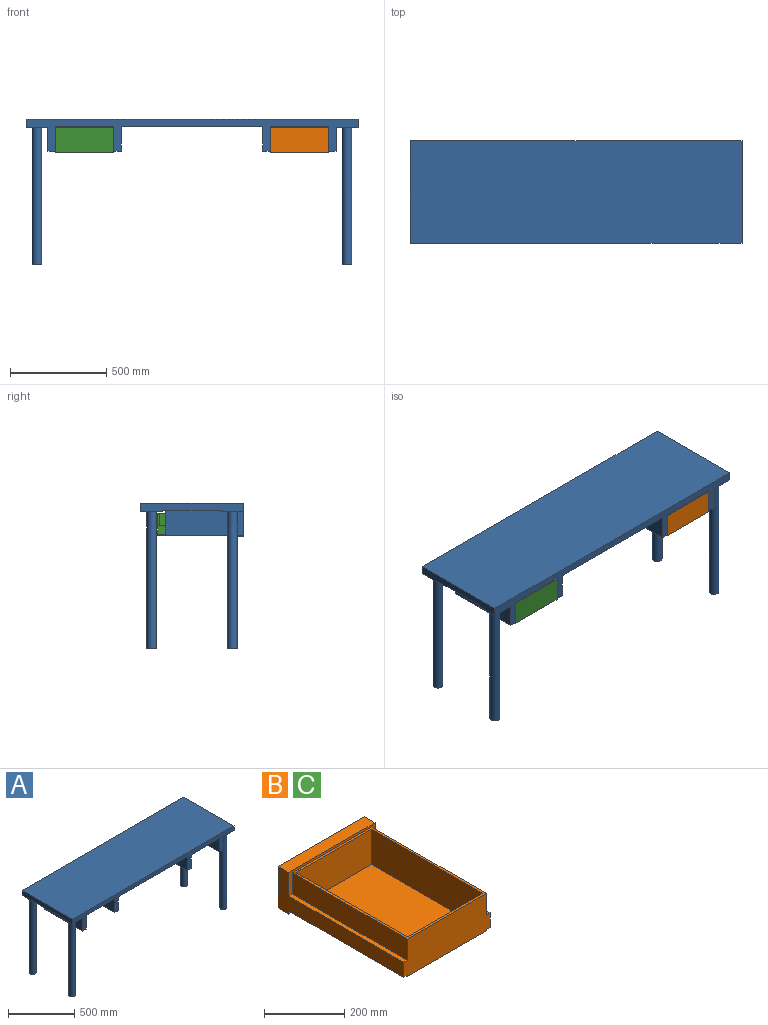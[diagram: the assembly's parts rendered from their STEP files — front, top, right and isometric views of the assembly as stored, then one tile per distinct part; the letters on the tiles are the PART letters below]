
ASSEMBLY  parts=3 mates=1
PART A: 40 faces, bbox 1727.2x533.4x755.7 mm
  f0: plane 406.4x127mm, normal (1,0,0), area 50887mm2, adj f1,f3,f15,f17,f18,f19
  f1: plane 1727.2x533.4mm, normal (0,0,-1), area 807095.2mm2, adj f0,f2,f3,f4,f5,f7,f11,f12
  f2: plane 533.4x44.45mm, normal (-1,0,0), area 21774.2mm2, adj f1,f3,f5,f6,f7,f8,f23,f24
  f3: plane 1727.2x165.1mm, normal (0,-1,0), area 86612.7mm2, adj f0,f1,f2,f4,f6,f8,f11,f13
  f4: plane 533.4x44.45mm, normal (1,0,0), area 21774.2mm2, adj f1,f3,f5,f6,f18,f19,f27,f29
  f5: plane 1727.2x44.45mm, normal (0,1,0), area 67257.9mm2, adj f1,f2,f4,f6,f22,f24,f28,f29
  f6: plane 1727.2x533.4mm, normal (0,0,1), area 921288.5mm2, adj f2,f3,f4,f5
  f7: plane 114.3x6.35mm, normal (0,1,0), area 725.8mm2, adj f1,f2,f8,f11
  f8: plane 114.3x114.3mm, normal (0,0,-1), area 11037.7mm2, adj f2,f3,f7,f9,f11
  f9: cylinder r=25.4mm len=711.2mm, axis (0,0,1), area 113502.5mm2, adj f8,f10
  f10: plane 50.8x50.8mm, normal (0,0,-1), area 2026.8mm2, adj f9
  f11: plane 406.4x127mm, normal (-1,0,0), area 50887mm2, adj f1,f3,f7,f8,f12,f14
  f12: plane 127x38.1mm, normal (0,1,0), area 4838.7mm2, adj f1,f11,f13,f14
  f13: plane 406.4x127mm, normal (1,0,0), area 51612.8mm2, adj f1,f3,f12,f14
  f14: plane 406.4x38.1mm, normal (0,0,-1), area 15483.8mm2, adj f3,f11,f12,f13
  f15: plane 127x38.1mm, normal (0,1,0), area 4838.7mm2, adj f0,f1,f16,f17
  f16: plane 406.4x127mm, normal (-1,0,0), area 51612.8mm2, adj f1,f3,f15,f17
  f17: plane 406.4x38.1mm, normal (0,0,-1), area 15483.8mm2, adj f0,f3,f15,f16
  f18: plane 114.3x6.35mm, normal (0,1,0), area 725.8mm2, adj f0,f1,f4,f19
  f19: plane 114.3x114.3mm, normal (0,0,-1), area 11037.7mm2, adj f0,f3,f4,f18,f20
  f20: cylinder r=25.4mm len=711.2mm, axis (0,0,1), area 113502.5mm2, adj f19,f21
  f21: plane 50.8x50.8mm, normal (0,0,-1), area 2026.8mm2, adj f20
  f22: plane 114.3x6.35mm, normal (1,0,0), area 725.8mm2, adj f1,f5,f23,f24
  f23: plane 114.3x6.35mm, normal (0,-1,0), area 725.8mm2, adj f1,f2,f22,f24
  f24: plane 114.3x114.3mm, normal (0,0,-1), area 11037.7mm2, adj f2,f5,f22,f23,f25
  f25: cylinder r=25.4mm len=711.2mm, axis (0,0,1), area 113502.5mm2, adj f24,f26
  f26: plane 50.8x50.8mm, normal (0,0,-1), area 2026.8mm2, adj f25
  f27: plane 114.3x6.35mm, normal (0,-1,0), area 725.8mm2, adj f1,f4,f28,f29
  f28: plane 114.3x6.35mm, normal (-1,0,0), area 725.8mm2, adj f1,f5,f27,f29
  f29: plane 114.3x114.3mm, normal (0,0,-1), area 11037.7mm2, adj f4,f5,f27,f28,f30
  f30: cylinder r=25.4mm len=711.2mm, axis (0,0,1), area 113502.5mm2, adj f29,f31
  f31: plane 50.8x50.8mm, normal (0,0,-1), area 2026.8mm2, adj f30
  f32: plane 406.4x127mm, normal (-1,0,0), area 51612.8mm2, adj f1,f3,f33,f35
  f33: plane 127x38.1mm, normal (0,1,0), area 4838.7mm2, adj f1,f32,f34,f35
  f34: plane 406.4x127mm, normal (1,0,0), area 51612.8mm2, adj f1,f3,f33,f35
  f35: plane 406.4x38.1mm, normal (0,0,-1), area 15483.8mm2, adj f3,f32,f33,f34
  f36: plane 406.4x127mm, normal (1,0,0), area 51612.8mm2, adj f1,f3,f38,f39
  f37: plane 406.4x127mm, normal (-1,0,0), area 51612.8mm2, adj f1,f3,f38,f39
  f38: plane 127x38.1mm, normal (0,1,0), area 4838.7mm2, adj f1,f36,f37,f39
  f39: plane 406.4x38.1mm, normal (0,0,-1), area 15483.8mm2, adj f3,f36,f37,f38
PART B: 23 faces, bbox 304.8x444.5x127 mm
  f0: plane 304.8x9.53mm, normal (0,-1,0), area 2016.1mm2, adj f1,f2,f4,f5,f6,f11,f19,f22
  f1: plane 406.4x3.18mm, normal (1,0,0), area 1290.3mm2, adj f0,f11,f13,f22
  f2: plane 406.4x3.18mm, normal (-1,0,0), area 1290.3mm2, adj f0,f11,f13,f19
  f3: plane 406.4x279.4mm, normal (0,0,1), area 8548.4mm2, adj f8,f10,f12,f13,f14,f15,f16,f17
  f4: plane 444.5x127mm, normal (-1,0,0), area 23419.3mm2, adj f0,f5,f7,f8,f9,f13,f19,f20
  f5: plane 304.8x38.1mm, normal (0,0,-1), area 11612.9mm2, adj f0,f4,f6,f9
  f6: plane 444.5x127mm, normal (1,0,0), area 23419.3mm2, adj f0,f5,f7,f8,f9,f13,f21,f22
  f7: plane 304.8x38.1mm, normal (0,0,1), area 11612.9mm2, adj f4,f6,f8,f9
  f8: plane 304.8x71.76mm, normal (0,-1,0), area 3596.8mm2, adj f3,f4,f6,f7,f10,f12,f20,f21
  f9: plane 304.8x127mm, normal (0,1,0), area 38709.6mm2, adj f4,f5,f6,f7
  f10: plane 406.4x65.41mm, normal (-1,0,0), area 26580.6mm2, adj f3,f8,f13,f20
  f11: plane 406.4x279.4mm, normal (0,0,-1), area 113548.2mm2, adj f0,f1,f2,f13
  f12: plane 406.4x65.41mm, normal (1,0,0), area 26580.6mm2, adj f3,f8,f13,f21
  f13: plane 304.8x114.3mm, normal (0,-1,0), area 33096.7mm2, adj f1,f2,f3,f4,f6,f10,f11,f12
  f14: plane 266.7x107.95mm, normal (0,1,0), area 28790.3mm2, adj f3,f15,f17,f18
  f15: plane 393.7x107.95mm, normal (-1,0,0), area 42499.9mm2, adj f3,f14,f16,f18
  f16: plane 266.7x107.95mm, normal (0,-1,0), area 28790.3mm2, adj f3,f15,f17,f18
  f17: plane 393.7x107.95mm, normal (1,0,0), area 42499.9mm2, adj f3,f14,f16,f18
  f18: plane 393.7x266.7mm, normal (0,0,1), area 104999.8mm2, adj f14,f15,f16,f17
  f19: plane 406.4x12.7mm, normal (0,0,-1), area 5161.3mm2, adj f0,f2,f4,f13
  f20: plane 406.4x12.7mm, normal (0,0,1), area 5161.3mm2, adj f4,f8,f10,f13
  f21: plane 406.4x12.7mm, normal (0,0,1), area 5161.3mm2, adj f6,f8,f12,f13
  f22: plane 406.4x12.7mm, normal (0,0,-1), area 5161.3mm2, adj f0,f1,f6,f13
PART C: same geometry as B
PLACE A t=(519.7,-444.47,641.99)mm
PLACE B rot(axis=(0,0,1),180deg) t=(2096.17,-444.47,508.87)mm
PLACE C rot(axis=(0,0,1),180deg) t=(978.57,-444.47,508.87)mm
MATE parallel C.f9 <-> A.f3  axis (0,-1,0) through (826.17,-444.47,572.37)mm
